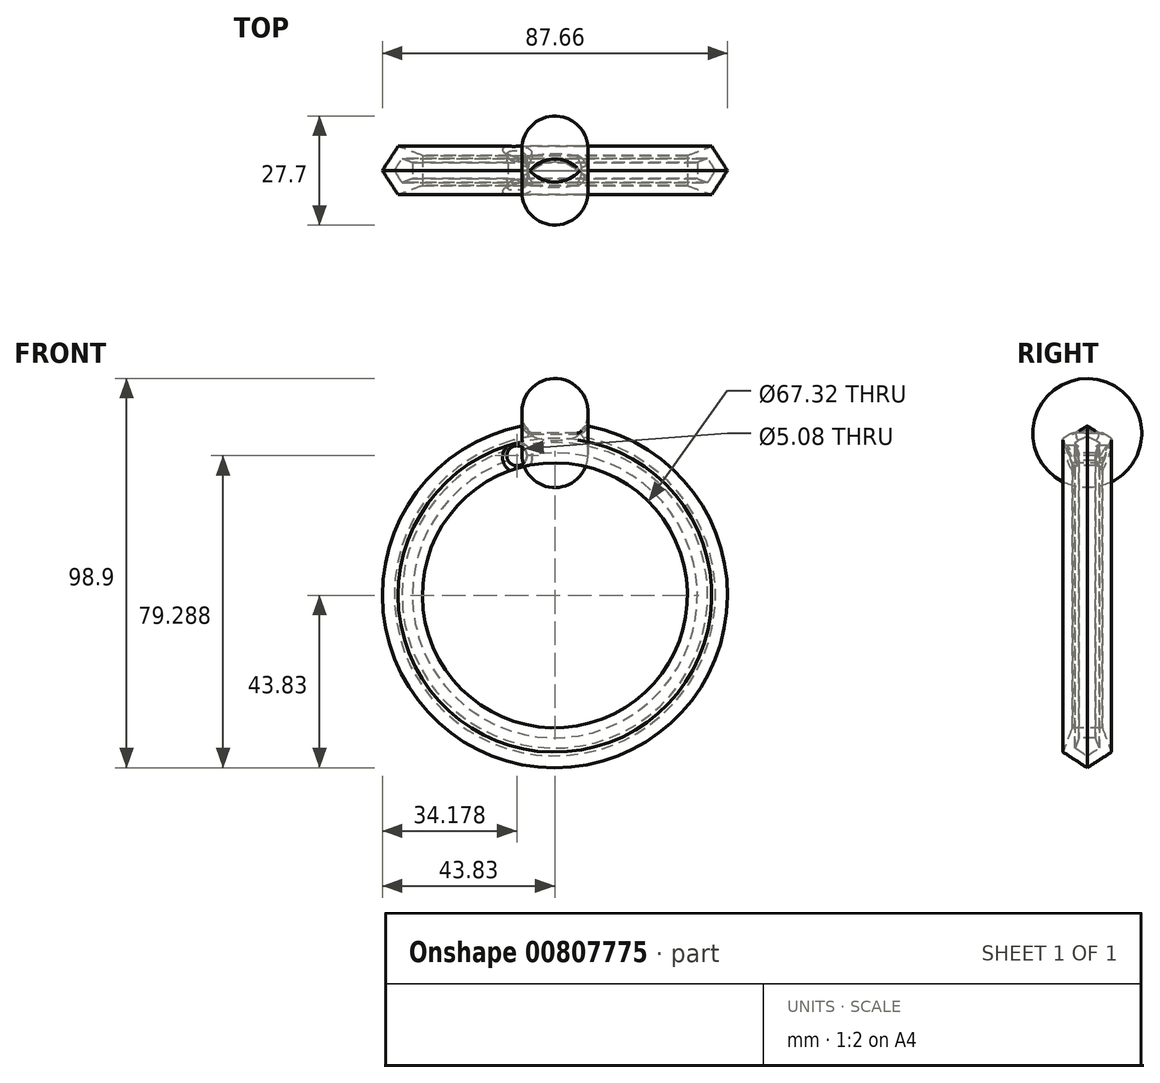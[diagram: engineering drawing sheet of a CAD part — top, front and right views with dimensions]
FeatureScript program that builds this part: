
annotation { "Feature Type Name" : "Feature", "Feature Type Description" : "" }
export const myFeature = defineFeature(function(context is Context, id is Id, definition is map)
    precondition{}
    {
        {
            var Q0;
            Q0=qCreatedBy(makeId("Front.planeOp"),FACE);
            var sketch = newSketch(context, id + "F0", { "sketchPlane" : qUnion([Q0])});
            skCircle(sketch, "E0", {"center": v(0, 0) * mm, "radius": 38.1 * mm});
            skSolve(sketch);
        }
        {
            var Q0;
            Q0=qCreatedBy(makeId("Top.planeOp"),FACE);
            cPlane(context, id + "F1", {"entities" : qUnion([Q0]), "cplaneType" : CPlaneType.OFFSET, "offset" : 19.05 * mm, "oppositeDirection" : true, "width" : 152.4 * mm, "height" : 152.4 * mm});
        }
        {
            var Q0;
            Q0=qCreatedBy(id+"F1.planeOp",FACE);
            var sketch = newSketch(context, id + "F2", { "sketchPlane" : qUnion([Q0])});
            skCircle(sketch, "E1.cCircle", {"center": v(-33, 0) * mm, "radius": 5.24 * mm, "construction": true});
            skLineSegment(sketch, "E1.0", {"start": v(-27.75, 3.81) * mm, "end": v(-27.75, -3.81) * mm});
            skLineSegment(sketch, "E1.1", {"start": v(-27.75, -3.81) * mm, "end": v(-35, -6.16) * mm});
            skLineSegment(sketch, "E1.2", {"start": v(-35, -6.16) * mm, "end": v(-39.48, 0) * mm});
            skLineSegment(sketch, "E1.3", {"start": v(-39.48, 0) * mm, "end": v(-35, 6.16) * mm});
            skLineSegment(sketch, "E1.4", {"start": v(-35, 6.16) * mm, "end": v(-27.75, 3.81) * mm});
            skPoint(sketch, "E1.0.midPoint", {"position": v(-27.75, 0) * mm});
            skSolve(sketch);
        }
        {
            var Q0;
            Q0=makeQuery(id+"F2.imprint","IMPRINT",FACE,{"disambiguationData":[TD([[makeQuery(id+"F2.imprint","IMPRINT",EDGE,{"derivedFrom":sQuery(id+"F2.wireOp",EDGE,"E1.0")}),-1.0]])]});
            var Q1;
            Q1=sQuery(id+"F0.wireOp",EDGE,"E0");
            sweep(context, id + "F3", {"profiles" : qUnion([Q0]), "path" : qUnion([Q1])});
        }
        {
            var Q0;
            Q0=makeQuery(id+"F3.opSweep","SWEPT_FACE",FACE,{"disambiguationData":[OSD([sQuery(id+"F0.wireOp",EDGE,"E0"),sQuery(id+"F2.wireOp",EDGE,"E1.0")])]});
            var Q1;
            Q1=makeQuery(id+"F3.opSweep","SWEPT_BODY",BODY,{"disambiguationData":[OSD([sQuery(id+"F0.wireOp",EDGE,"E0"),sQuery(id+"F2.wireOp",EDGE,"E1.0"),sQuery(id+"F2.wireOp",EDGE,"E1.1"),sQuery(id+"F2.wireOp",EDGE,"E1.2"),sQuery(id+"F2.wireOp",EDGE,"E1.3"),sQuery(id+"F2.wireOp",EDGE,"E1.4")])]});
            shell(context, id + "F4", {"isHollow" : true, "entities" : qUnion([Q0]), "parts" : qUnion([Q1]), "thickness" : 2.54 * mm});
        }
        {
            var Q0;
            Q0=qCreatedBy(makeId("Front.planeOp"),FACE);
            var sketch = newSketch(context, id + "F5", { "sketchPlane" : qUnion([Q0])});
            skCircle(sketch, "E2", {"center": v(-9.65, 35.46) * mm, "radius": 2.54 * mm});
            skSolve(sketch);
        }
        {
            var Q0;
            Q0 = qSketchRegion(id + "F5", true);
            extrude(context, id + "F6", {"entities" : qUnion([Q0]), "operationType" : NewBodyOperationType.REMOVE, "endBound" : BoundingType.SYMMETRIC, "oppositeDirection" : true, "depth" : 25.4 * mm, "offsetDistance" : 25.4 * mm});
        }
        {
            var Q0;
            Q0=qCreatedBy(makeId("Front.planeOp"),FACE);
            var sketch = newSketch(context, id + "F7", { "sketchPlane" : qUnion([Q0])});
            skCircle(sketch, "E3.cCircle", {"center": v(0, 52.22) * mm, "radius": 11 * mm, "construction": true});
            skLineSegment(sketch, "E3.0", {"start": v(6.35, 41.22) * mm, "end": v(-6.35, 41.22) * mm});
            skLineSegment(sketch, "E3.1", {"start": v(-6.35, 41.22) * mm, "end": v(-12.7, 52.22) * mm});
            skLineSegment(sketch, "E3.2", {"start": v(-12.7, 52.22) * mm, "end": v(-6.35, 63.21) * mm});
            skLineSegment(sketch, "E3.3", {"start": v(-6.35, 63.21) * mm, "end": v(6.35, 63.21) * mm});
            skLineSegment(sketch, "E3.4", {"start": v(6.35, 63.21) * mm, "end": v(12.7, 52.22) * mm});
            skLineSegment(sketch, "E3.5", {"start": v(12.7, 52.22) * mm, "end": v(6.35, 41.22) * mm});
            skPoint(sketch, "E3.0.midPoint", {"position": v(0, 41.22) * mm});
            skSolve(sketch);
        }
        {
            var Q0;
            Q0 = qSketchRegion(id + "F7", true);
            extrude(context, id + "F8", {"entities" : qUnion([Q0]), "operationType" : NewBodyOperationType.REMOVE, "endBound" : BoundingType.SYMMETRIC, "oppositeDirection" : true, "depth" : 25.4 * mm, "offsetDistance" : 25.4 * mm});
        }
        {
            var Q0;
            Q0=makeQuery(id+"F8.boolean.opBoolean","COPY",FACE,{"derivedFrom":makeQuery(id+"F8.opExtrude","SWEPT_FACE",FACE,{"disambiguationData":[OSD([sQuery(id+"F7.wireOp",EDGE,"E3.0")])]})});
            var sketch = newSketch(context, id + "F9", { "sketchPlane" : qUnion([Q0])});
            skArc(sketch, "E4", {"start": v(6.35, 0) * mm, "mid": v(0, 2.91) * mm, "end": v(-6.35, 0) * mm});
            skLineSegment(sketch, "E5", {"start": v(6.35, 0) * mm, "end": v(-6.35, 0) * mm});
            skSolve(sketch);
        }
        {
            var Q0;
            Q0 = qSketchRegion(id + "F9", true);
            var Q1;
            Q1=sQuery(id+"F9.wireOp",EDGE,"E5");
            revolve(context, id + "F10", {"operationType" : NewBodyOperationType.REMOVE, "surfaceOperationType" : NewSurfaceOperationType.NEW, "entities" : qUnion([Q0]), "axis" : qUnion([Q1]), "revolveType" : RevolveType.FULL, "oppositeDirection" : true});
        }
        {
            var Q0;
            Q0=makeQuery(id+"F6.boolean.opBoolean","INTERSECT",EDGE,{"derivedFrom":[makeQuery(id+"F3.opSweep","SWEPT_FACE",FACE,{"disambiguationData":[OSD([sQuery(id+"F0.wireOp",EDGE,"E0"),sQuery(id+"F2.wireOp",EDGE,"E1.4")])]}),makeQuery(id+"F6.opExtrude","SWEPT_FACE",FACE,{"disambiguationData":[OSD([sQuery(id+"F5.wireOp",EDGE,"E2")])]})]});
            var Q1;
            Q1=makeQuery(id+"FTETRIm0HSytxBk_1.1.F6.boolean.opBoolean","INTERSECT",EDGE,{"derivedFrom":[makeQuery(id+"F3.opSweep","SWEPT_FACE",FACE,{"disambiguationData":[OSD([sQuery(id+"F0.wireOp",EDGE,"E0"),sQuery(id+"F2.wireOp",EDGE,"E1.4")])]}),makeQuery(id+"FTETRIm0HSytxBk_1.1.F6.opExtrude","SWEPT_FACE",FACE,{"disambiguationData":[OSD([sQuery(id+"F5.wireOp",EDGE,"E2")])]})]});
            var Q2;
            Q2=makeQuery(id+"FTETRIm0HSytxBk_1.11.F6.boolean.opBoolean","INTERSECT",EDGE,{"derivedFrom":[makeQuery(id+"F3.opSweep","SWEPT_FACE",FACE,{"disambiguationData":[OSD([sQuery(id+"F0.wireOp",EDGE,"E0"),sQuery(id+"F2.wireOp",EDGE,"E1.4")])]}),makeQuery(id+"FTETRIm0HSytxBk_1.11.F6.opExtrude","SWEPT_FACE",FACE,{"disambiguationData":[OSD([sQuery(id+"F5.wireOp",EDGE,"E2")])]})]});
            var Q3;
            Q3=makeQuery(id+"FTETRIm0HSytxBk_1.10.F6.boolean.opBoolean","INTERSECT",EDGE,{"derivedFrom":[makeQuery(id+"F3.opSweep","SWEPT_FACE",FACE,{"disambiguationData":[OSD([sQuery(id+"F0.wireOp",EDGE,"E0"),sQuery(id+"F2.wireOp",EDGE,"E1.4")])]}),makeQuery(id+"FTETRIm0HSytxBk_1.10.F6.opExtrude","SWEPT_FACE",FACE,{"disambiguationData":[OSD([sQuery(id+"F5.wireOp",EDGE,"E2")])]})]});
            var Q4;
            Q4=makeQuery(id+"FTETRIm0HSytxBk_1.9.F6.boolean.opBoolean","INTERSECT",EDGE,{"derivedFrom":[makeQuery(id+"F3.opSweep","SWEPT_FACE",FACE,{"disambiguationData":[OSD([sQuery(id+"F0.wireOp",EDGE,"E0"),sQuery(id+"F2.wireOp",EDGE,"E1.4")])]}),makeQuery(id+"FTETRIm0HSytxBk_1.9.F6.opExtrude","SWEPT_FACE",FACE,{"disambiguationData":[OSD([sQuery(id+"F5.wireOp",EDGE,"E2")])]})]});
            var Q5;
            Q5=makeQuery(id+"FTETRIm0HSytxBk_1.2.F6.boolean.opBoolean","INTERSECT",EDGE,{"derivedFrom":[makeQuery(id+"F3.opSweep","SWEPT_FACE",FACE,{"disambiguationData":[OSD([sQuery(id+"F0.wireOp",EDGE,"E0"),sQuery(id+"F2.wireOp",EDGE,"E1.4")])]}),makeQuery(id+"FTETRIm0HSytxBk_1.2.F6.opExtrude","SWEPT_FACE",FACE,{"disambiguationData":[OSD([sQuery(id+"F5.wireOp",EDGE,"E2")])]})]});
            var Q6;
            Q6=makeQuery(id+"FTETRIm0HSytxBk_1.3.F6.boolean.opBoolean","INTERSECT",EDGE,{"derivedFrom":[makeQuery(id+"F3.opSweep","SWEPT_FACE",FACE,{"disambiguationData":[OSD([sQuery(id+"F0.wireOp",EDGE,"E0"),sQuery(id+"F2.wireOp",EDGE,"E1.4")])]}),makeQuery(id+"FTETRIm0HSytxBk_1.3.F6.opExtrude","SWEPT_FACE",FACE,{"disambiguationData":[OSD([sQuery(id+"F5.wireOp",EDGE,"E2")])]})]});
            var Q7;
            Q7=makeQuery(id+"FTETRIm0HSytxBk_1.4.F6.boolean.opBoolean","INTERSECT",EDGE,{"derivedFrom":[makeQuery(id+"F3.opSweep","SWEPT_FACE",FACE,{"disambiguationData":[OSD([sQuery(id+"F0.wireOp",EDGE,"E0"),sQuery(id+"F2.wireOp",EDGE,"E1.4")])]}),makeQuery(id+"FTETRIm0HSytxBk_1.4.F6.opExtrude","SWEPT_FACE",FACE,{"disambiguationData":[OSD([sQuery(id+"F5.wireOp",EDGE,"E2")])]})]});
            var Q8;
            Q8=makeQuery(id+"FTETRIm0HSytxBk_1.5.F6.boolean.opBoolean","INTERSECT",EDGE,{"derivedFrom":[makeQuery(id+"F3.opSweep","SWEPT_FACE",FACE,{"disambiguationData":[OSD([sQuery(id+"F0.wireOp",EDGE,"E0"),sQuery(id+"F2.wireOp",EDGE,"E1.4")])]}),makeQuery(id+"FTETRIm0HSytxBk_1.5.F6.opExtrude","SWEPT_FACE",FACE,{"disambiguationData":[OSD([sQuery(id+"F5.wireOp",EDGE,"E2")])]})]});
            var Q9;
            Q9=makeQuery(id+"FTETRIm0HSytxBk_1.6.F6.boolean.opBoolean","INTERSECT",EDGE,{"derivedFrom":[makeQuery(id+"F3.opSweep","SWEPT_FACE",FACE,{"disambiguationData":[OSD([sQuery(id+"F0.wireOp",EDGE,"E0"),sQuery(id+"F2.wireOp",EDGE,"E1.4")])]}),makeQuery(id+"FTETRIm0HSytxBk_1.6.F6.opExtrude","SWEPT_FACE",FACE,{"disambiguationData":[OSD([sQuery(id+"F5.wireOp",EDGE,"E2")])]})]});
            var Q10;
            Q10=makeQuery(id+"FTETRIm0HSytxBk_1.7.F6.boolean.opBoolean","INTERSECT",EDGE,{"derivedFrom":[makeQuery(id+"F3.opSweep","SWEPT_FACE",FACE,{"disambiguationData":[OSD([sQuery(id+"F0.wireOp",EDGE,"E0"),sQuery(id+"F2.wireOp",EDGE,"E1.4")])]}),makeQuery(id+"FTETRIm0HSytxBk_1.7.F6.opExtrude","SWEPT_FACE",FACE,{"disambiguationData":[OSD([sQuery(id+"F5.wireOp",EDGE,"E2")])]})]});
            var Q11;
            Q11=makeQuery(id+"FTETRIm0HSytxBk_1.8.F6.boolean.opBoolean","INTERSECT",EDGE,{"derivedFrom":[makeQuery(id+"F3.opSweep","SWEPT_FACE",FACE,{"disambiguationData":[OSD([sQuery(id+"F0.wireOp",EDGE,"E0"),sQuery(id+"F2.wireOp",EDGE,"E1.4")])]}),makeQuery(id+"FTETRIm0HSytxBk_1.8.F6.opExtrude","SWEPT_FACE",FACE,{"disambiguationData":[OSD([sQuery(id+"F5.wireOp",EDGE,"E2")])]})]});
            var Q12;
            Q12=makeQuery(id+"FTETRIm0HSytxBk_1.7.F6.boolean.opBoolean","INTERSECT",EDGE,{"derivedFrom":[makeQuery(id+"F3.opSweep","SWEPT_FACE",FACE,{"disambiguationData":[OSD([sQuery(id+"F0.wireOp",EDGE,"E0"),sQuery(id+"F2.wireOp",EDGE,"E1.1")])]}),makeQuery(id+"FTETRIm0HSytxBk_1.7.F6.opExtrude","SWEPT_FACE",FACE,{"disambiguationData":[OSD([sQuery(id+"F5.wireOp",EDGE,"E2")])]})]});
            var Q13;
            Q13=makeQuery(id+"FTETRIm0HSytxBk_1.8.F6.boolean.opBoolean","INTERSECT",EDGE,{"derivedFrom":[makeQuery(id+"F3.opSweep","SWEPT_FACE",FACE,{"disambiguationData":[OSD([sQuery(id+"F0.wireOp",EDGE,"E0"),sQuery(id+"F2.wireOp",EDGE,"E1.1")])]}),makeQuery(id+"FTETRIm0HSytxBk_1.8.F6.opExtrude","SWEPT_FACE",FACE,{"disambiguationData":[OSD([sQuery(id+"F5.wireOp",EDGE,"E2")])]})]});
            var Q14;
            Q14=makeQuery(id+"FTETRIm0HSytxBk_1.9.F6.boolean.opBoolean","INTERSECT",EDGE,{"derivedFrom":[makeQuery(id+"F3.opSweep","SWEPT_FACE",FACE,{"disambiguationData":[OSD([sQuery(id+"F0.wireOp",EDGE,"E0"),sQuery(id+"F2.wireOp",EDGE,"E1.1")])]}),makeQuery(id+"FTETRIm0HSytxBk_1.9.F6.opExtrude","SWEPT_FACE",FACE,{"disambiguationData":[OSD([sQuery(id+"F5.wireOp",EDGE,"E2")])]})]});
            var Q15;
            Q15=makeQuery(id+"FTETRIm0HSytxBk_1.6.F6.boolean.opBoolean","INTERSECT",EDGE,{"derivedFrom":[makeQuery(id+"F3.opSweep","SWEPT_FACE",FACE,{"disambiguationData":[OSD([sQuery(id+"F0.wireOp",EDGE,"E0"),sQuery(id+"F2.wireOp",EDGE,"E1.1")])]}),makeQuery(id+"FTETRIm0HSytxBk_1.6.F6.opExtrude","SWEPT_FACE",FACE,{"disambiguationData":[OSD([sQuery(id+"F5.wireOp",EDGE,"E2")])]})]});
            var Q16;
            Q16=makeQuery(id+"FTETRIm0HSytxBk_1.5.F6.boolean.opBoolean","INTERSECT",EDGE,{"derivedFrom":[makeQuery(id+"F3.opSweep","SWEPT_FACE",FACE,{"disambiguationData":[OSD([sQuery(id+"F0.wireOp",EDGE,"E0"),sQuery(id+"F2.wireOp",EDGE,"E1.1")])]}),makeQuery(id+"FTETRIm0HSytxBk_1.5.F6.opExtrude","SWEPT_FACE",FACE,{"disambiguationData":[OSD([sQuery(id+"F5.wireOp",EDGE,"E2")])]})]});
            var Q17;
            Q17=makeQuery(id+"FTETRIm0HSytxBk_1.4.F6.boolean.opBoolean","INTERSECT",EDGE,{"derivedFrom":[makeQuery(id+"F3.opSweep","SWEPT_FACE",FACE,{"disambiguationData":[OSD([sQuery(id+"F0.wireOp",EDGE,"E0"),sQuery(id+"F2.wireOp",EDGE,"E1.1")])]}),makeQuery(id+"FTETRIm0HSytxBk_1.4.F6.opExtrude","SWEPT_FACE",FACE,{"disambiguationData":[OSD([sQuery(id+"F5.wireOp",EDGE,"E2")])]})]});
            var Q18;
            Q18=makeQuery(id+"FTETRIm0HSytxBk_1.10.F6.boolean.opBoolean","INTERSECT",EDGE,{"derivedFrom":[makeQuery(id+"F3.opSweep","SWEPT_FACE",FACE,{"disambiguationData":[OSD([sQuery(id+"F0.wireOp",EDGE,"E0"),sQuery(id+"F2.wireOp",EDGE,"E1.1")])]}),makeQuery(id+"FTETRIm0HSytxBk_1.10.F6.opExtrude","SWEPT_FACE",FACE,{"disambiguationData":[OSD([sQuery(id+"F5.wireOp",EDGE,"E2")])]})]});
            var Q19;
            Q19=makeQuery(id+"FTETRIm0HSytxBk_1.11.F6.boolean.opBoolean","INTERSECT",EDGE,{"derivedFrom":[makeQuery(id+"F3.opSweep","SWEPT_FACE",FACE,{"disambiguationData":[OSD([sQuery(id+"F0.wireOp",EDGE,"E0"),sQuery(id+"F2.wireOp",EDGE,"E1.1")])]}),makeQuery(id+"FTETRIm0HSytxBk_1.11.F6.opExtrude","SWEPT_FACE",FACE,{"disambiguationData":[OSD([sQuery(id+"F5.wireOp",EDGE,"E2")])]})]});
            var Q20;
            Q20=makeQuery(id+"F6.boolean.opBoolean","INTERSECT",EDGE,{"derivedFrom":[makeQuery(id+"F3.opSweep","SWEPT_FACE",FACE,{"disambiguationData":[OSD([sQuery(id+"F0.wireOp",EDGE,"E0"),sQuery(id+"F2.wireOp",EDGE,"E1.1")])]}),makeQuery(id+"F6.opExtrude","SWEPT_FACE",FACE,{"disambiguationData":[OSD([sQuery(id+"F5.wireOp",EDGE,"E2")])]})]});
            var Q21;
            Q21=makeQuery(id+"FTETRIm0HSytxBk_1.1.F6.boolean.opBoolean","INTERSECT",EDGE,{"derivedFrom":[makeQuery(id+"F3.opSweep","SWEPT_FACE",FACE,{"disambiguationData":[OSD([sQuery(id+"F0.wireOp",EDGE,"E0"),sQuery(id+"F2.wireOp",EDGE,"E1.1")])]}),makeQuery(id+"FTETRIm0HSytxBk_1.1.F6.opExtrude","SWEPT_FACE",FACE,{"disambiguationData":[OSD([sQuery(id+"F5.wireOp",EDGE,"E2")])]})]});
            var Q22;
            Q22=makeQuery(id+"FTETRIm0HSytxBk_1.2.F6.boolean.opBoolean","INTERSECT",EDGE,{"derivedFrom":[makeQuery(id+"F3.opSweep","SWEPT_FACE",FACE,{"disambiguationData":[OSD([sQuery(id+"F0.wireOp",EDGE,"E0"),sQuery(id+"F2.wireOp",EDGE,"E1.1")])]}),makeQuery(id+"FTETRIm0HSytxBk_1.2.F6.opExtrude","SWEPT_FACE",FACE,{"disambiguationData":[OSD([sQuery(id+"F5.wireOp",EDGE,"E2")])]})]});
            var Q23;
            Q23=makeQuery(id+"FTETRIm0HSytxBk_1.3.F6.boolean.opBoolean","INTERSECT",EDGE,{"derivedFrom":[makeQuery(id+"F3.opSweep","SWEPT_FACE",FACE,{"disambiguationData":[OSD([sQuery(id+"F0.wireOp",EDGE,"E0"),sQuery(id+"F2.wireOp",EDGE,"E1.1")])]}),makeQuery(id+"FTETRIm0HSytxBk_1.3.F6.opExtrude","SWEPT_FACE",FACE,{"disambiguationData":[OSD([sQuery(id+"F5.wireOp",EDGE,"E2")])]})]});
            var Q24;
            Q24=makeQuery(id+"FFUxmemCmtagzyA_1.4.F8.boolean.opBoolean","INTERSECT",EDGE,{"derivedFrom":[makeQuery(id+"F3.opSweep","SWEPT_FACE",FACE,{"disambiguationData":[OSD([sQuery(id+"F0.wireOp",EDGE,"E0"),sQuery(id+"F2.wireOp",EDGE,"E1.3")])]}),makeQuery(id+"FFUxmemCmtagzyA_1.4.F8.opExtrude","SWEPT_FACE",FACE,{"disambiguationData":[OSD([sQuery(id+"F7.wireOp",EDGE,"E3.0")])]})]});
            var Q25;
            Q25=makeQuery(id+"FFUxmemCmtagzyA_1.4.F8.boolean.opBoolean","INTERSECT",EDGE,{"derivedFrom":[makeQuery(id+"F3.opSweep","SWEPT_FACE",FACE,{"disambiguationData":[OSD([sQuery(id+"F0.wireOp",EDGE,"E0"),sQuery(id+"F2.wireOp",EDGE,"E1.2")])]}),makeQuery(id+"FFUxmemCmtagzyA_1.4.F8.opExtrude","SWEPT_FACE",FACE,{"disambiguationData":[OSD([sQuery(id+"F7.wireOp",EDGE,"E3.0")])]})]});
            var Q26;
            Q26=makeQuery(id+"FFUxmemCmtagzyA_1.4.F8.boolean.opBoolean","COPY",FACE,{"derivedFrom":makeQuery(id+"FFUxmemCmtagzyA_1.4.F8.opExtrude","SWEPT_FACE",FACE,{"disambiguationData":[OSD([sQuery(id+"F7.wireOp",EDGE,"E3.1")])]})});
            var Q27;
            Q27=makeQuery(id+"FFUxmemCmtagzyA_1.4.F8.boolean.opBoolean","COPY",FACE,{"derivedFrom":makeQuery(id+"FFUxmemCmtagzyA_1.4.F8.opExtrude","SWEPT_FACE",FACE,{"disambiguationData":[OSD([sQuery(id+"F7.wireOp",EDGE,"E3.5")])]})});
            var Q28;
            Q28=makeQuery(id+"F8.boolean.opBoolean","COPY",FACE,{"derivedFrom":makeQuery(id+"F8.opExtrude","SWEPT_FACE",FACE,{"disambiguationData":[OSD([sQuery(id+"F7.wireOp",EDGE,"E3.5")])]})});
            var Q29;
            Q29=makeQuery(id+"F8.boolean.opBoolean","INTERSECT",EDGE,{"derivedFrom":[makeQuery(id+"F3.opSweep","SWEPT_FACE",FACE,{"disambiguationData":[OSD([sQuery(id+"F0.wireOp",EDGE,"E0"),sQuery(id+"F2.wireOp",EDGE,"E1.3")])]}),makeQuery(id+"F8.opExtrude","SWEPT_FACE",FACE,{"disambiguationData":[OSD([sQuery(id+"F7.wireOp",EDGE,"E3.0")])]})]});
            var Q30;
            Q30=makeQuery(id+"F8.boolean.opBoolean","INTERSECT",EDGE,{"derivedFrom":[makeQuery(id+"F3.opSweep","SWEPT_FACE",FACE,{"disambiguationData":[OSD([sQuery(id+"F0.wireOp",EDGE,"E0"),sQuery(id+"F2.wireOp",EDGE,"E1.2")])]}),makeQuery(id+"F8.opExtrude","SWEPT_FACE",FACE,{"disambiguationData":[OSD([sQuery(id+"F7.wireOp",EDGE,"E3.0")])]})]});
            var Q31;
            Q31=makeQuery(id+"F8.boolean.opBoolean","COPY",FACE,{"derivedFrom":makeQuery(id+"F8.opExtrude","SWEPT_FACE",FACE,{"disambiguationData":[OSD([sQuery(id+"F7.wireOp",EDGE,"E3.1")])]})});
            var Q32;
            Q32=makeQuery(id+"FFUxmemCmtagzyA_1.1.F8.boolean.opBoolean","COPY",FACE,{"derivedFrom":makeQuery(id+"FFUxmemCmtagzyA_1.1.F8.opExtrude","SWEPT_FACE",FACE,{"disambiguationData":[OSD([sQuery(id+"F7.wireOp",EDGE,"E3.5")])]})});
            var Q33;
            Q33=makeQuery(id+"FFUxmemCmtagzyA_1.1.F8.boolean.opBoolean","INTERSECT",EDGE,{"derivedFrom":[makeQuery(id+"F3.opSweep","SWEPT_FACE",FACE,{"disambiguationData":[OSD([sQuery(id+"F0.wireOp",EDGE,"E0"),sQuery(id+"F2.wireOp",EDGE,"E1.2")])]}),makeQuery(id+"FFUxmemCmtagzyA_1.1.F8.opExtrude","SWEPT_FACE",FACE,{"disambiguationData":[OSD([sQuery(id+"F7.wireOp",EDGE,"E3.0")])]})]});
            var Q34;
            Q34=makeQuery(id+"FFUxmemCmtagzyA_1.1.F8.boolean.opBoolean","INTERSECT",EDGE,{"derivedFrom":[makeQuery(id+"F3.opSweep","SWEPT_FACE",FACE,{"disambiguationData":[OSD([sQuery(id+"F0.wireOp",EDGE,"E0"),sQuery(id+"F2.wireOp",EDGE,"E1.3")])]}),makeQuery(id+"FFUxmemCmtagzyA_1.1.F8.opExtrude","SWEPT_FACE",FACE,{"disambiguationData":[OSD([sQuery(id+"F7.wireOp",EDGE,"E3.0")])]})]});
            var Q35;
            Q35=makeQuery(id+"FFUxmemCmtagzyA_1.1.F8.boolean.opBoolean","COPY",FACE,{"derivedFrom":makeQuery(id+"FFUxmemCmtagzyA_1.1.F8.opExtrude","SWEPT_FACE",FACE,{"disambiguationData":[OSD([sQuery(id+"F7.wireOp",EDGE,"E3.1")])]})});
            var Q36;
            Q36=makeQuery(id+"FFUxmemCmtagzyA_1.2.F8.boolean.opBoolean","COPY",FACE,{"derivedFrom":makeQuery(id+"FFUxmemCmtagzyA_1.2.F8.opExtrude","SWEPT_FACE",FACE,{"disambiguationData":[OSD([sQuery(id+"F7.wireOp",EDGE,"E3.5")])]})});
            var Q37;
            Q37=makeQuery(id+"FFUxmemCmtagzyA_1.2.F8.boolean.opBoolean","COPY",FACE,{"derivedFrom":makeQuery(id+"FFUxmemCmtagzyA_1.2.F8.opExtrude","SWEPT_FACE",FACE,{"disambiguationData":[OSD([sQuery(id+"F7.wireOp",EDGE,"E3.1")])]})});
            var Q38;
            Q38=makeQuery(id+"FFUxmemCmtagzyA_1.3.F8.boolean.opBoolean","COPY",FACE,{"derivedFrom":makeQuery(id+"FFUxmemCmtagzyA_1.3.F8.opExtrude","SWEPT_FACE",FACE,{"disambiguationData":[OSD([sQuery(id+"F7.wireOp",EDGE,"E3.5")])]})});
            var Q39;
            Q39=makeQuery(id+"FFUxmemCmtagzyA_1.3.F8.boolean.opBoolean","COPY",FACE,{"derivedFrom":makeQuery(id+"FFUxmemCmtagzyA_1.3.F8.opExtrude","SWEPT_FACE",FACE,{"disambiguationData":[OSD([sQuery(id+"F7.wireOp",EDGE,"E3.1")])]})});
            fillet(context, id + "F11", {"entities" : qUnion([Q0, Q1, Q2, Q3, Q4, Q5, Q6, Q7, Q8, Q9, Q10, Q11, Q12, Q13, Q14, Q15, Q16, Q17, Q18, Q19, Q20, Q21, Q22, Q23, Q24, Q25, Q26, Q27, Q28, Q29, Q30, Q31, Q32, Q33, Q34, Q35, Q36, Q37, Q38, Q39]), "radius" : 1.27 * mm, "tangentPropagation" : true, "allowEdgeOverflow" : false});
        }
    });
